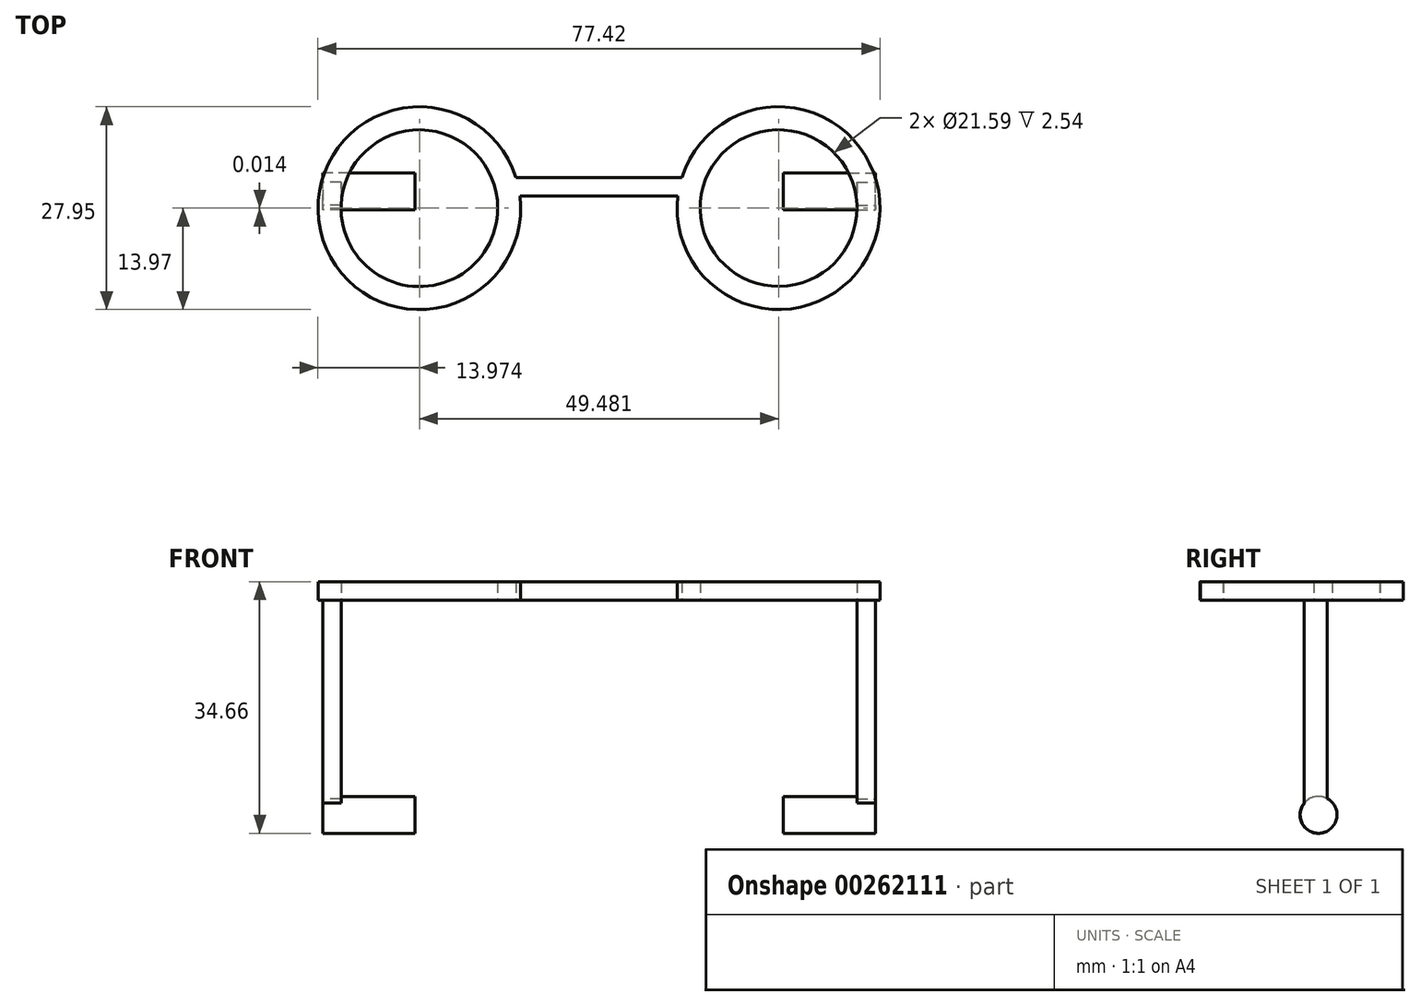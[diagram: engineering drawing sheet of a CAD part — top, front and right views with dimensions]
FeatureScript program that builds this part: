
annotation { "Feature Type Name" : "Feature", "Feature Type Description" : "" }
export const myFeature = defineFeature(function(context is Context, id is Id, definition is map)
    precondition{}
    {
        {
            var Q0;
            Q0=qCreatedBy(makeId("Top.planeOp"),FACE);
            var sketch = newSketch(context, id + "F0", { "sketchPlane" : qUnion([Q0])});
            skArc(sketch, "E0", {"start": v(-48.84, 37.29) * mm, "mid": v(-75.8, 30.05) * mm, "end": v(-48.28, 34.75) * mm});
            skArc(sketch, "E1", {"start": v(-26.53, 34.75) * mm, "mid": v(0.98, 30.08) * mm, "end": v(-25.98, 37.29) * mm});
            skCircle(sketch, "E2", {"center": v(-62.15, 33.04) * mm, "radius": 10.8 * mm});
            skCircle(sketch, "E3", {"center": v(-12.67, 33.05) * mm, "radius": 10.8 * mm});
            skLineSegment(sketch, "E4", {"start": v(-48.84, 37.29) * mm, "end": v(-25.98, 37.29) * mm});
            skLineSegment(sketch, "E5", {"start": v(-48.28, 34.75) * mm, "end": v(-26.53, 34.75) * mm});
            skSolve(sketch);
        }
        {
            var Q0;
            Q0 = qSketchRegion(id + "F0", true);
            extrude(context, id + "F1", {"entities" : qUnion([Q0]), "depth" : 2.54 * mm});
        }
        {
            var Q0;
            Q0=makeQuery(id+"F1.opExtrude","CAP_FACE",FACE,{"disambiguationData":[OSD([sQuery(id+"F0.wireOp",EDGE,"E0"),sQuery(id+"F0.wireOp",EDGE,"E1"),sQuery(id+"F0.wireOp",EDGE,"E2"),sQuery(id+"F0.wireOp",EDGE,"E3"),sQuery(id+"F0.wireOp",EDGE,"E4"),sQuery(id+"F0.wireOp",EDGE,"E5")])],"isStart":true});
            var sketch = newSketch(context, id + "F2", { "sketchPlane" : qUnion([Q0])});
            skLineSegment(sketch, "E6.bottom", {"start": v(-72.93, -33.42) * mm, "end": v(-75.47, -33.42) * mm});
            skLineSegment(sketch, "E6.top", {"start": v(-72.93, -36.6) * mm, "end": v(-75.47, -36.6) * mm});
            skLineSegment(sketch, "E6.left", {"start": v(-72.93, -33.42) * mm, "end": v(-72.93, -36.6) * mm});
            skLineSegment(sketch, "E6.right", {"start": v(-75.47, -33.42) * mm, "end": v(-75.47, -36.6) * mm});
            skPoint(sketch, "E6.middle", {"position": v(-74.2, -35) * mm});
            skLineSegment(sketch, "E7", {"start": v(-37.4, -37.29) * mm, "end": v(-37.4, -19.01) * mm});
            skLineSegment(sketch, "E8", {"start": v(-37.4, -19.01) * mm, "end": v(-37.4, -50.4) * mm});
            skLineSegment(sketch, "E9.MirrorCS", {"start": v(-1.88, -36.6) * mm, "end": v(0.66, -36.6) * mm});
            skLineSegment(sketch, "E10.MirrorCS", {"start": v(0.66, -33.42) * mm, "end": v(0.66, -36.6) * mm});
            skLineSegment(sketch, "E11.MirrorCS", {"start": v(-1.88, -33.42) * mm, "end": v(0.66, -33.42) * mm});
            skLineSegment(sketch, "E12.MirrorCS", {"start": v(-1.88, -33.42) * mm, "end": v(-1.88, -36.6) * mm});
            skSolve(sketch);
        }
        {
            var Q0;
            Q0 = qSketchRegion(id + "F2", true);
            extrude(context, id + "F3", {"entities" : qUnion([Q0]), "operationType" : NewBodyOperationType.ADD, "depth" : 27.94 * mm});
        }
        {
            var Q0;
            Q0=makeQuery(id+"F3.opExtrude","SWEPT_FACE",FACE,{"disambiguationData":[OSD([sQuery(id+"F2.wireOp",EDGE,"E6.right")])]});
            var sketch = newSketch(context, id + "F4", { "sketchPlane" : qUnion([Q0])});
            skCircle(sketch, "E13", {"center": v(-35.36, -29.58) * mm, "radius": 2.54 * mm});
            skSolve(sketch);
        }
        {
            var Q0;
            Q0 = qSketchRegion(id + "F4", true);
            extrude(context, id + "F5", {"entities" : qUnion([Q0]), "operationType" : NewBodyOperationType.ADD, "oppositeDirection" : true, "depth" : 12.7 * mm});
        }
        {
            var Q0;
            Q0=makeQuery(id+"F3.opExtrude","SWEPT_FACE",FACE,{"disambiguationData":[OSD([sQuery(id+"F2.wireOp",EDGE,"E10.MirrorCS")])]});
            var sketch = newSketch(context, id + "F6", { "sketchPlane" : qUnion([Q0])});
            skCircle(sketch, "E14", {"center": v(35.38, -29.57) * mm, "radius": 2.54 * mm});
            skSolve(sketch);
        }
        {
            var Q0;
            Q0 = qSketchRegion(id + "F6", true);
            extrude(context, id + "F7", {"entities" : qUnion([Q0]), "operationType" : NewBodyOperationType.ADD, "oppositeDirection" : true, "depth" : 12.7 * mm});
        }
    });
